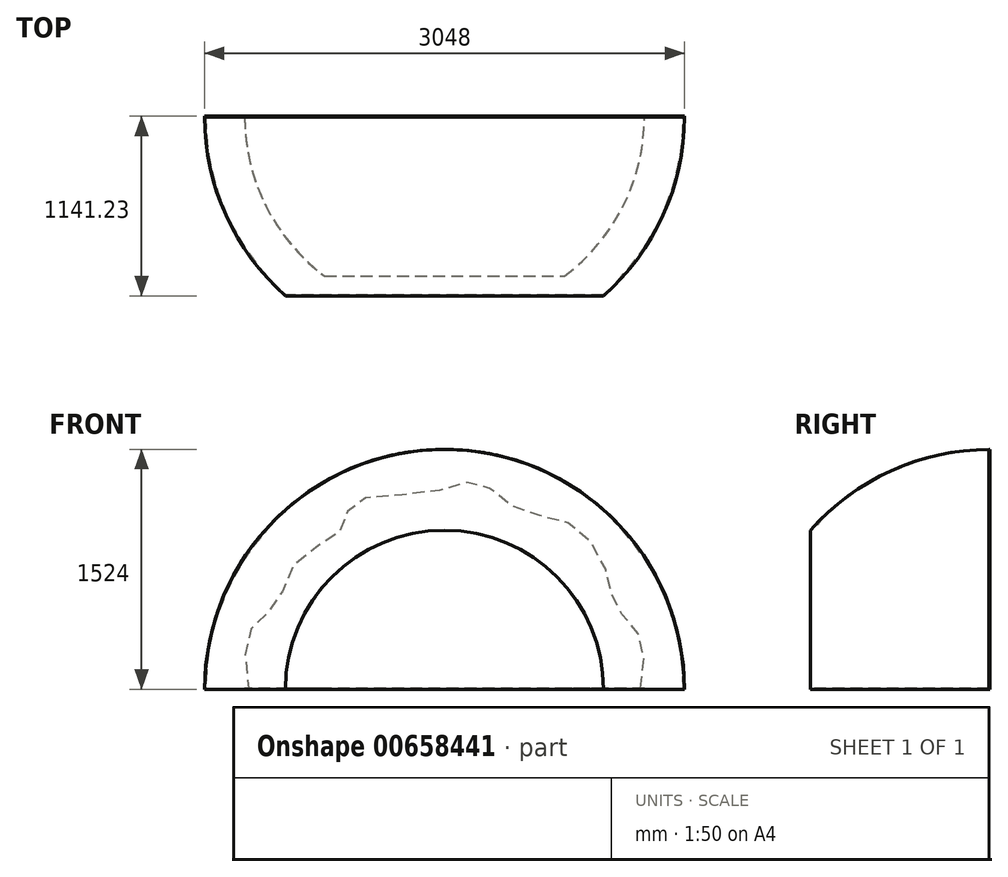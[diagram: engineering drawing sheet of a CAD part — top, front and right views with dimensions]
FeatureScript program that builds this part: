
annotation { "Feature Type Name" : "Feature", "Feature Type Description" : "" }
export const myFeature = defineFeature(function(context is Context, id is Id, definition is map)
    precondition{}
    {
        {
            var Q0;
            Q0=qCreatedBy(makeId("Front.planeOp"),FACE);
            var sketch = newSketch(context, id + "F0", { "sketchPlane" : qUnion([Q0])});
            skArc(sketch, "E0", {"start": v(0, 1524) * mm, "mid": v(-1077.63, 1077.63) * mm, "end": v(-1524, 0) * mm});
            skLineSegment(sketch, "E1", {"start": v(-1524, 0) * mm, "end": v(0, 0) * mm});
            skLineSegment(sketch, "E2", {"start": v(0, 0) * mm, "end": v(0, 1524) * mm});
            skSolve(sketch);
        }
        {
            var Q0;
            Q0=makeQuery(id+"F0.imprint","IMPRINT",FACE,{"disambiguationData":[TD([[makeQuery(id+"F0.imprint","IMPRINT",EDGE,{"derivedFrom":sQuery(id+"F0.wireOp",EDGE,"E0")}),1.0]])]});
            var Q1;
            Q1=sQuery(id+"F0.wireOp",EDGE,"E2");
            revolve(context, id + "F1", {"entities" : qUnion([Q0]), "axis" : qUnion([Q1]), "revolveType" : RevolveType.ONE_DIRECTION, "angle" : 180 * degree});
        }
        {
            var Q0;
            Q0=qCreatedBy(makeId("Right.planeOp"),FACE);
            var sketch = newSketch(context, id + "F2", { "sketchPlane" : qUnion([Q0])});
            skLineSegment(sketch, "E3.bottom", {"start": v(-1583.4, 0) * mm, "end": v(-1141.23, 0) * mm});
            skLineSegment(sketch, "E3.top", {"start": v(-1583.4, 1745.94) * mm, "end": v(-1141.23, 1745.94) * mm});
            skLineSegment(sketch, "E3.left", {"start": v(-1583.4, 0) * mm, "end": v(-1583.4, 1745.94) * mm});
            skLineSegment(sketch, "E3.right", {"start": v(-1141.23, 0) * mm, "end": v(-1141.23, 1745.94) * mm});
            skSolve(sketch);
        }
        {
            var Q0;
            Q0=makeQuery(id+"F2.imprint","IMPRINT",FACE,{"disambiguationData":[TD([[makeQuery(id+"F2.imprint","IMPRINT",EDGE,{"derivedFrom":sQuery(id+"F2.wireOp",EDGE,"E3.bottom")}),1.0]])]});
            extrude(context, id + "F3", {"entities" : qUnion([Q0]), "operationType" : NewBodyOperationType.REMOVE, "endBound" : BoundingType.SYMMETRIC, "depth" : 5080 * mm, "offsetDistance" : 25.4 * mm});
        }
        {
            var Q0;
            Q0=makeQuery(id+"F1.opRevolve","CAP_FACE",FACE,{"disambiguationData":[OSD([sQuery(id+"F0.wireOp",EDGE,"E0"),sQuery(id+"F0.wireOp",EDGE,"E1"),sQuery(id+"F0.wireOp",EDGE,"E2")])],"isStart":true});
            shell(context, id + "F4", {"entities" : qUnion([Q0]), "thickness" : 6.35 * mm});
        }
        {
            var Q0;
            Q0=qCreatedBy(makeId("Front.planeOp"),FACE);
            var sketch = newSketch(context, id + "F5", { "sketchPlane" : qUnion([Q0])});
            skArc(sketch, "E4", {"start": v(1524, 0) * mm, "mid": v(0, 1524) * mm, "end": v(-1524, 0) * mm});
            skLineSegment(sketch, "E5", {"start": v(1524, 0) * mm, "end": v(1244.6, 0) * mm});
            skLineSegment(sketch, "E6", {"start": v(-1244.6, 0) * mm, "end": v(-1524, 0) * mm});
            skFitSpline(sketch, "E7", {"points": [v(1244.6, 0) * mm, v(1244.6, 326.66) * mm, v(1094.51, 520.33) * mm, v(1029.34, 745.03) * mm, v(811.39, 1043.96) * mm, v(468.94, 1142.57) * mm, v(216.33, 1311.79) * mm, v(-98.56, 1249.82) * mm, v(-581.3, 1182.9) * mm, v(-658.38, 1009.25) * mm, v(-932.66, 820.38) * mm, v(-1066.21, 546.35) * mm, v(-1235.86, 370.55) * mm, v(-1244.6, 0) * mm], "startDerivative": vector(741.8, 4533.55) * mm, "endDerivative": vector(698.12, -5048.08) * mm});
            skSolve(sketch);
        }
        {
            var Q0;
            Q0=makeQuery(id+"F5.imprint","IMPRINT",FACE,{"disambiguationData":[TD([[makeQuery(id+"F5.imprint","IMPRINT",EDGE,{"derivedFrom":sQuery(id+"F5.wireOp",EDGE,"E4")}),1.0]])]});
            extrude(context, id + "F6", {"entities" : qUnion([Q0]), "operationType" : NewBodyOperationType.ADD, "depth" : 6.35 * mm, "offsetDistance" : 25.4 * mm});
        }
        {
            var Q0;
            Q0=makeQuery(id+"F6.boolean.opBoolean","MERGE",FACE,{"derivedFrom":[makeQuery(id+"F1.opRevolve","SWEPT_FACE",FACE,{"disambiguationData":[OSD([sQuery(id+"F0.wireOp",EDGE,"E1")])]}),makeQuery(id+"F6.opExtrude","SWEPT_FACE",FACE,{"disambiguationData":[OSD([sQuery(id+"F5.wireOp",EDGE,"E5")])]}),makeQuery(id+"F6.opExtrude","SWEPT_FACE",FACE,{"disambiguationData":[OSD([sQuery(id+"F5.wireOp",EDGE,"E6")])]})]});
            var sketch = newSketch(context, id + "F7", { "sketchPlane" : qUnion([Q0])});
            skArc(sketch, "E8", {"start": v(1270, 0) * mm, "mid": v(1135.92, 567.96) * mm, "end": v(762, 1016) * mm});
            skLineSegment(sketch, "E9", {"start": v(-762, 1016) * mm, "end": v(762, 1016) * mm});
            skLineSegment(sketch, "E10", {"start": v(-1270, 0) * mm, "end": v(1270, 0) * mm});
            skArc(sketch, "E11.trimOffspring", {"start": v(-762, 1016) * mm, "mid": v(-1135.92, 567.96) * mm, "end": v(-1270, 0) * mm});
            skSolve(sketch);
        }
        {
            var Q0;
            Q0 = qSketchRegion(id + "F7", true);
            extrude(context, id + "F8", {"entities" : qUnion([Q0]), "operationType" : NewBodyOperationType.REMOVE, "oppositeDirection" : true, "depth" : 6.35 * mm, "offsetDistance" : 25.4 * mm});
        }
    });
